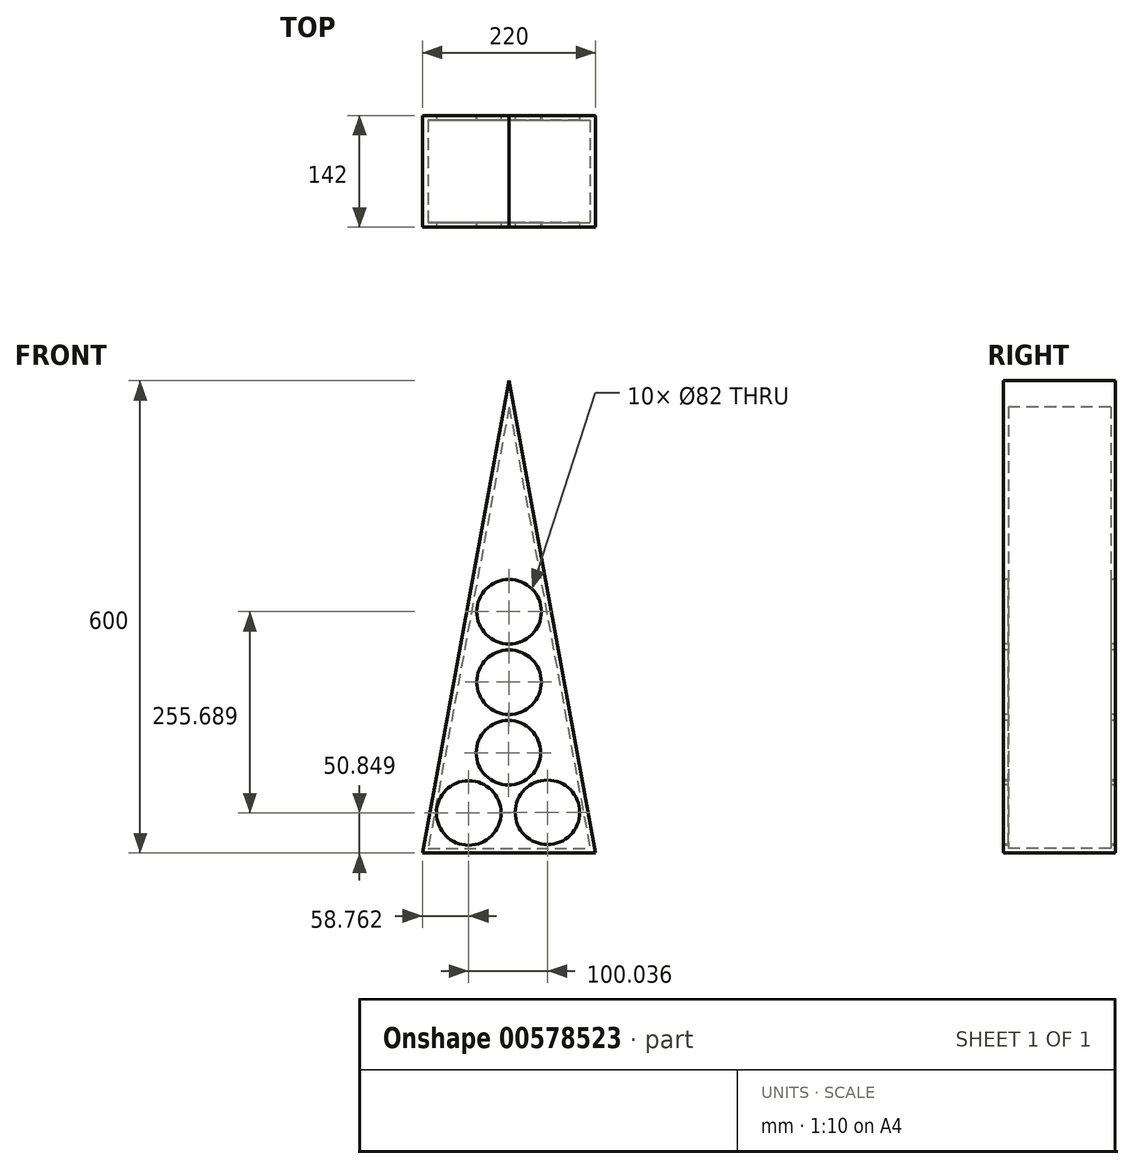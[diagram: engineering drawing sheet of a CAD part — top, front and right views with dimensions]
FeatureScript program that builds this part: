
annotation { "Feature Type Name" : "Feature", "Feature Type Description" : "" }
export const myFeature = defineFeature(function(context is Context, id is Id, definition is map)
    precondition{}
    {
        {
            var Q0;
            Q0=qCreatedBy(makeId("Front.planeOp"),FACE);
            var sketch = newSketch(context, id + "F0", { "sketchPlane" : qUnion([Q0])});
            skLineSegment(sketch, "E0", {"start": v(0, 0) * mm, "end": v(110, 0) * mm});
            skLineSegment(sketch, "E1", {"start": v(0, 0) * mm, "end": v(-110, 0) * mm});
            skLineSegment(sketch, "E2", {"start": v(-110, 0) * mm, "end": v(0, 600) * mm});
            skLineSegment(sketch, "E3", {"start": v(0, 600) * mm, "end": v(110, 0) * mm});
            skSolve(sketch);
        }
        {
            var Q0;
            Q0=makeQuery(id+"F0.imprint","IMPRINT",FACE,{"disambiguationData":[TD([[makeQuery(id+"F0.imprint","IMPRINT",EDGE,{"derivedFrom":sQuery(id+"F0.wireOp",EDGE,"E0")}),1.0]])]});
            extrude(context, id + "F1", {"entities" : qUnion([Q0]), "depth" : 6 * mm, "offsetDistance" : 25.4 * mm});
        }
        {
            var Q0;
            Q0=makeQuery(id+"F1.opExtrude","CAP_FACE",FACE,{"disambiguationData":[OSD([sQuery(id+"F0.wireOp",EDGE,"E0"),sQuery(id+"F0.wireOp",EDGE,"E1"),sQuery(id+"F0.wireOp",EDGE,"E2"),sQuery(id+"F0.wireOp",EDGE,"E3")])],"isStart":true});
            var sketch = newSketch(context, id + "F2", { "sketchPlane" : qUnion([Q0])});
            skLineSegment(sketch, "E4", {"start": v(106.47, 19.27) * mm, "end": v(0, 600) * mm});
            skLineSegment(sketch, "E5", {"start": v(106.47, 19.27) * mm, "end": v(110, 0) * mm});
            skLineSegment(sketch, "E6", {"start": v(0, 566.73) * mm, "end": v(88.48, 84.1) * mm});
            skLineSegment(sketch, "E7", {"start": v(88.48, 84.1) * mm, "end": v(103.9, 0) * mm});
            skLineSegment(sketch, "E8", {"start": v(0, 566.73) * mm, "end": v(-3.05, 583.36) * mm});
            skLineSegment(sketch, "E9", {"start": v(-3.05, 583.36) * mm, "end": v(0, 600) * mm});
            skLineSegment(sketch, "E10", {"start": v(110, 0) * mm, "end": v(103.9, 0) * mm});
            skSolve(sketch);
        }
        {
            var Q0;
            Q0=makeQuery(id+"F2.imprint","IMPRINT",FACE,{"disambiguationData":[TD([[makeQuery(id+"F2.imprint","IMPRINT",EDGE,{"derivedFrom":sQuery(id+"F2.wireOp",EDGE,"E4")}),1.0]])]});
            extrude(context, id + "F3", {"entities" : qUnion([Q0]), "operationType" : NewBodyOperationType.ADD, "depth" : 130 * mm, "offsetDistance" : 25.4 * mm});
        }
        {
            var Q0;
            Q0=makeQuery(id+"F1.opExtrude","CAP_FACE",FACE,{"disambiguationData":[OSD([sQuery(id+"F0.wireOp",EDGE,"E0"),sQuery(id+"F0.wireOp",EDGE,"E1"),sQuery(id+"F0.wireOp",EDGE,"E2"),sQuery(id+"F0.wireOp",EDGE,"E3")])],"isStart":true});
            var sketch = newSketch(context, id + "F4", { "sketchPlane" : qUnion([Q0])});
            skLineSegment(sketch, "E11", {"start": v(-3.05, 583.36) * mm, "end": v(-110, 0) * mm});
            skLineSegment(sketch, "E12", {"start": v(0, 566.73) * mm, "end": v(-101.4, 13.62) * mm});
            skLineSegment(sketch, "E13", {"start": v(-101.4, 13.62) * mm, "end": v(-103.9, 0) * mm});
            skLineSegment(sketch, "E14", {"start": v(-110, 0) * mm, "end": v(-103.9, 0) * mm});
            skLineSegment(sketch, "E15", {"start": v(0, 566.73) * mm, "end": v(-3.05, 583.36) * mm});
            skSolve(sketch);
        }
        {
            var Q0;
            Q0 = qSketchRegion(id + "F4", true);
            extrude(context, id + "F5", {"entities" : qUnion([Q0]), "operationType" : NewBodyOperationType.ADD, "depth" : 130 * mm, "offsetDistance" : 25.4 * mm});
        }
        {
            var Q0;
            Q0=makeQuery(id+"F1.opExtrude","CAP_FACE",FACE,{"disambiguationData":[OSD([sQuery(id+"F0.wireOp",EDGE,"E0"),sQuery(id+"F0.wireOp",EDGE,"E1"),sQuery(id+"F0.wireOp",EDGE,"E2"),sQuery(id+"F0.wireOp",EDGE,"E3")])],"isStart":true});
            var sketch = newSketch(context, id + "F6", { "sketchPlane" : qUnion([Q0])});
            skLineSegment(sketch, "E16", {"start": v(-103.9, 0) * mm, "end": v(103.9, 0) * mm});
            skLineSegment(sketch, "E17", {"start": v(94.24, 6) * mm, "end": v(-89.78, 6) * mm});
            skLineSegment(sketch, "E18", {"start": v(-89.78, 6) * mm, "end": v(-102.8, 6) * mm});
            skLineSegment(sketch, "E19", {"start": v(-102.8, 6) * mm, "end": v(-103.9, 0) * mm});
            skLineSegment(sketch, "E20", {"start": v(94.24, 6) * mm, "end": v(102.8, 6) * mm});
            skLineSegment(sketch, "E21", {"start": v(102.8, 6) * mm, "end": v(103.9, 0) * mm});
            skSolve(sketch);
        }
        {
            var Q0;
            Q0 = qSketchRegion(id + "F6", true);
            extrude(context, id + "F7", {"entities" : qUnion([Q0]), "operationType" : NewBodyOperationType.ADD, "depth" : 130 * mm, "offsetDistance" : 25.4 * mm});
        }
        {
            var Q0;
            Q0=makeQuery(id+"F7.boolean.opBoolean","MERGE",FACE,{"derivedFrom":[makeQuery(id+"F5.boolean.opBoolean","MERGE",FACE,{"derivedFrom":[makeQuery(id+"F3.opExtrude","CAP_FACE",FACE,{"disambiguationData":[OSD([sQuery(id+"F2.wireOp",EDGE,"E4"),sQuery(id+"F2.wireOp",EDGE,"E5"),sQuery(id+"F2.wireOp",EDGE,"E6"),sQuery(id+"F2.wireOp",EDGE,"E7"),sQuery(id+"F2.wireOp",EDGE,"E8"),sQuery(id+"F2.wireOp",EDGE,"E9"),sQuery(id+"F2.wireOp",EDGE,"E10")])],"isStart":false}),makeQuery(id+"F5.opExtrude","CAP_FACE",FACE,{"disambiguationData":[OSD([sQuery(id+"F4.wireOp",EDGE,"E11"),sQuery(id+"F4.wireOp",EDGE,"E12"),sQuery(id+"F4.wireOp",EDGE,"E13"),sQuery(id+"F4.wireOp",EDGE,"E14"),sQuery(id+"F4.wireOp",EDGE,"E15")])],"isStart":false})]}),makeQuery(id+"F7.opExtrude","CAP_FACE",FACE,{"disambiguationData":[OSD([sQuery(id+"F6.wireOp",EDGE,"E16"),sQuery(id+"F6.wireOp",EDGE,"E17"),sQuery(id+"F6.wireOp",EDGE,"E18"),sQuery(id+"F6.wireOp",EDGE,"E19"),sQuery(id+"F6.wireOp",EDGE,"E20"),sQuery(id+"F6.wireOp",EDGE,"E21")])],"isStart":false})]});
            var sketch = newSketch(context, id + "F8", { "sketchPlane" : qUnion([Q0])});
            skLineSegment(sketch, "E22", {"start": v(0, 600) * mm, "end": v(110, 0) * mm});
            skLineSegment(sketch, "E23", {"start": v(110, 0) * mm, "end": v(-110, 0) * mm});
            skLineSegment(sketch, "E24", {"start": v(-110, 0) * mm, "end": v(0, 600) * mm});
            skSolve(sketch);
        }
        {
            var Q0;
            Q0 = qSketchRegion(id + "F8", true);
            extrude(context, id + "F9", {"entities" : qUnion([Q0]), "operationType" : NewBodyOperationType.ADD, "depth" : 6 * mm, "offsetDistance" : 25.4 * mm});
        }
        {
            var Q0;
            Q0=makeQuery(id+"F1.opExtrude","CAP_FACE",FACE,{"disambiguationData":[OSD([sQuery(id+"F0.wireOp",EDGE,"E0"),sQuery(id+"F0.wireOp",EDGE,"E1"),sQuery(id+"F0.wireOp",EDGE,"E2"),sQuery(id+"F0.wireOp",EDGE,"E3")])],"isStart":false});
            var sketch = newSketch(context, id + "F10", { "sketchPlane" : qUnion([Q0])});
            skCircle(sketch, "E25", {"center": v(48.8, 51.66) * mm, "radius": 41 * mm});
            skCircle(sketch, "E26", {"center": v(-51.24, 50.85) * mm, "radius": 41 * mm});
            skCircle(sketch, "E27", {"center": v(-0.81, 127.3) * mm, "radius": 41 * mm});
            skCircle(sketch, "E28", {"center": v(0, 217.07) * mm, "radius": 41 * mm});
            skCircle(sketch, "E29", {"center": v(0, 306.54) * mm, "radius": 41 * mm});
            skSolve(sketch);
        }
        {
            var Q0;
            Q0 = qSketchRegion(id + "F10", true);
            extrude(context, id + "F11", {"entities" : qUnion([Q0]), "operationType" : NewBodyOperationType.REMOVE, "oppositeDirection" : true, "depth" : 309.88 * mm, "offsetDistance" : 25.4 * mm});
        }
    });
